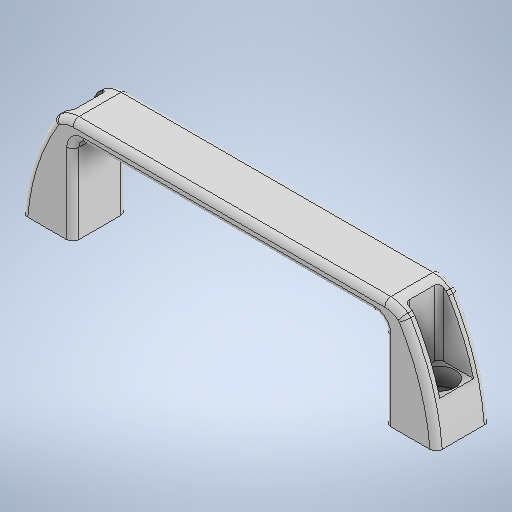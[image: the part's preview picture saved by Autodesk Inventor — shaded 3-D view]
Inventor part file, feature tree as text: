
AUTODESK INVENTOR PART (.ipt)
format: ipt  version: 2025 (Build 290162000, 162)  size: 342,528 bytes
history: native  units: mm
features: sketch x3, extrude x2, fillet x2, hole x1, mirror x1
ambient origin geometry x8: Origin, YZ Plane, XZ Plane, XY Plane, X Axis, Y Axis, Z Axis, Center Point
bodies: Solid1 (feature_tree)
feature tree (9):
  extrude  "Extrusion1"  Depth=8.0mm
  fillet  "Fillet1"  Radius=5.0mm
  fillet  "Fillet2"  Radius=152.0mm
  extrude  "Extrusion2"  Depth=3.0mm
  hole  "Hole1"  [1 undecoded]
  mirror  "Mirror1"
  sketch  "Sketch1"  dims[d1=44.0mm d2=8.0mm d4=5.0mm d5=152.0mm]
  sketch  "Sketch2"  dims[d6=26.5mm d7=0.0mm d8=3.0mm]
  sketch  "Sketch3"  dims[d9=3.0mm d10=5.0mm d11=5.0mm d12=5.0mm d13=5.0mm d14=2.0mm d15=5.0mm d16=2.0mm d17=33.0mm d18=0.0mm d19=8.0mm d20=6.0mm d21=15.0mm d22=8.6mm d23=90.0deg d24=8.0mm d25=20.594885mm d27=89.694mm]
note: 1 required parameter value undecoded (feature->parameter linkage not recoverable at this tier; creation-order binding heuristic only, values carry confidence <= 0.55)
